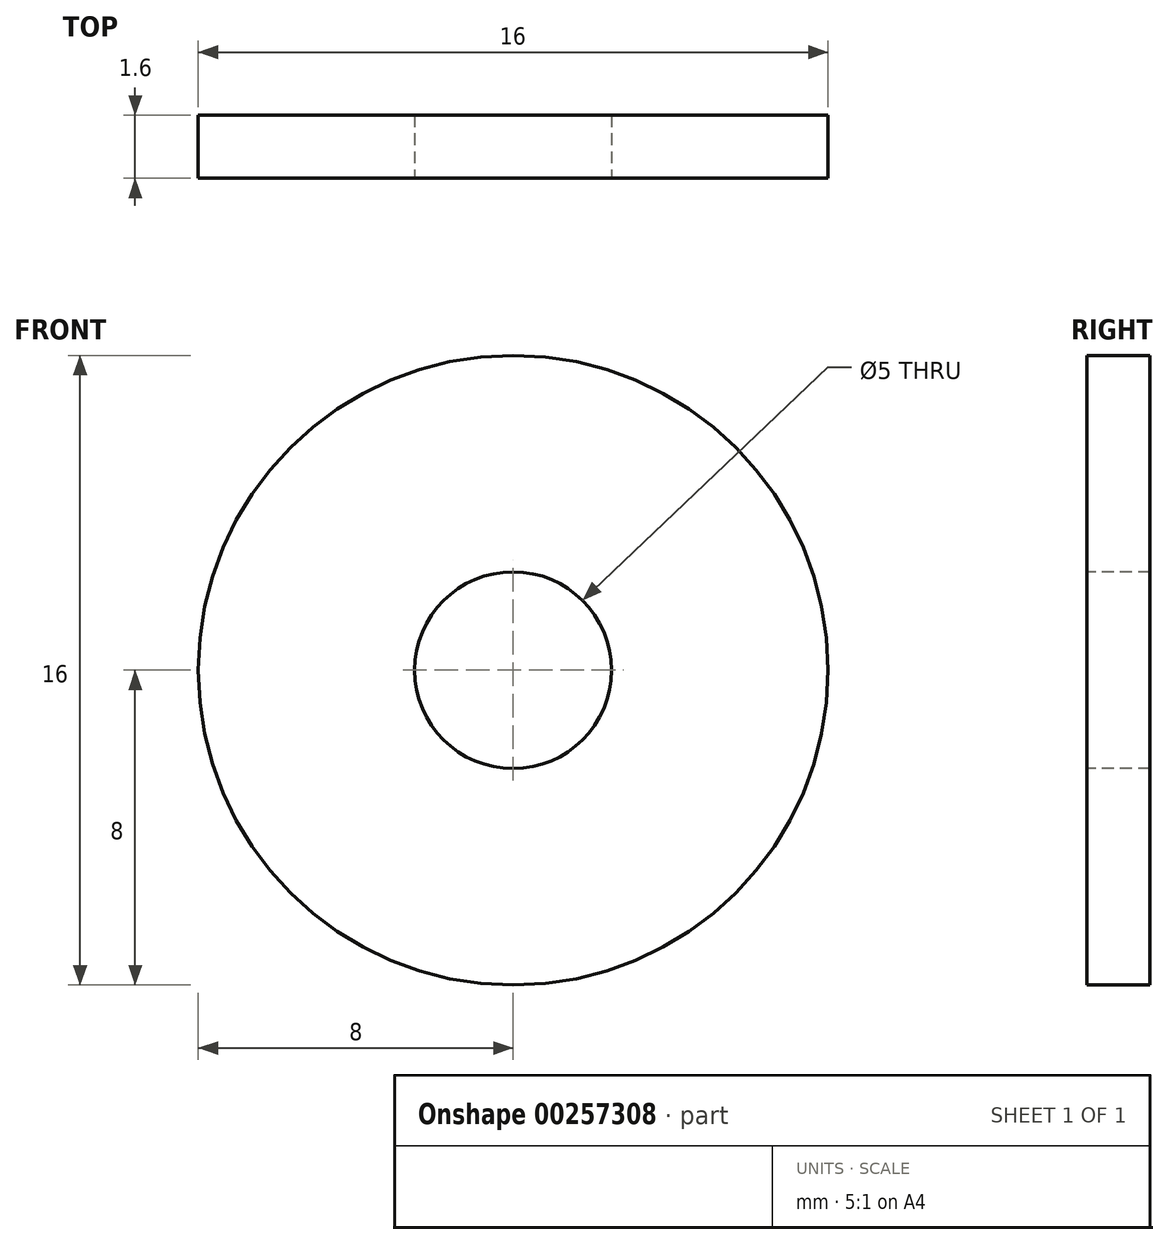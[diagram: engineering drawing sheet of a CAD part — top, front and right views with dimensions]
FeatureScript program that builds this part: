
annotation { "Feature Type Name" : "Feature", "Feature Type Description" : "" }
export const myFeature = defineFeature(function(context is Context, id is Id, definition is map)
    precondition{}
    {
        {
            var Q0;
            Q0=qCreatedBy(makeId("Front.planeOp"),FACE);
            var sketch = newSketch(context, id + "F0", { "sketchPlane" : qUnion([Q0])});
            skCircle(sketch, "E0", {"center": v(0, 0) * mm, "radius": 8 * mm});
            skSolve(sketch);
        }
        {
            var Q0;
            Q0=makeQuery(id+"F0.imprint","IMPRINT",FACE,{"disambiguationData":[TD([[makeQuery(id+"F0.imprint","IMPRINT",EDGE,{"derivedFrom":sQuery(id+"F0.wireOp",EDGE,"E0")}),1.0]])]});
            extrude(context, id + "F1", {"entities" : qUnion([Q0]), "oppositeDirection" : true, "depth" : 1.6 * mm});
        }
        {
            var Q0;
            Q0=sQuery(id+"F0.wireOp",VERTEX,"E0.center");
            var Q1;
            Q1=makeQuery(id+"F1.opExtrude","SWEPT_BODY",BODY,{"disambiguationData":[OSD([sQuery(id+"F0.wireOp",EDGE,"E0")])]});
            hole(context, id + "F2", {"style" : HoleStyle.SIMPLE, "endStyle" : HoleEndStyle.THROUGH, "standardTappedOrClearance" : lookupTablePath({ "standard" : "ISO", "fit" : "Normal", "engagement" : "75%", "pitch" : "1 mm", "size" : "M6", "type" : "Tapped" }), "standardBlindInLast" : lookupTablePath({ "fit" : "Standard", "standard" : "ISO", "engagement" : "75%", "pitch" : "1 mm", "size" : "M6", "type" : "Tapped" }), "holeDiameter" : 5 * mm, "showTappedDepth" : true, "tappedDepth" : 12 * mm, "tapClearance" : 3, "locations" : qUnion([Q0]), "scope" : qUnion([Q1]), "majorDiameter" : 6 * mm});
        }
    });
